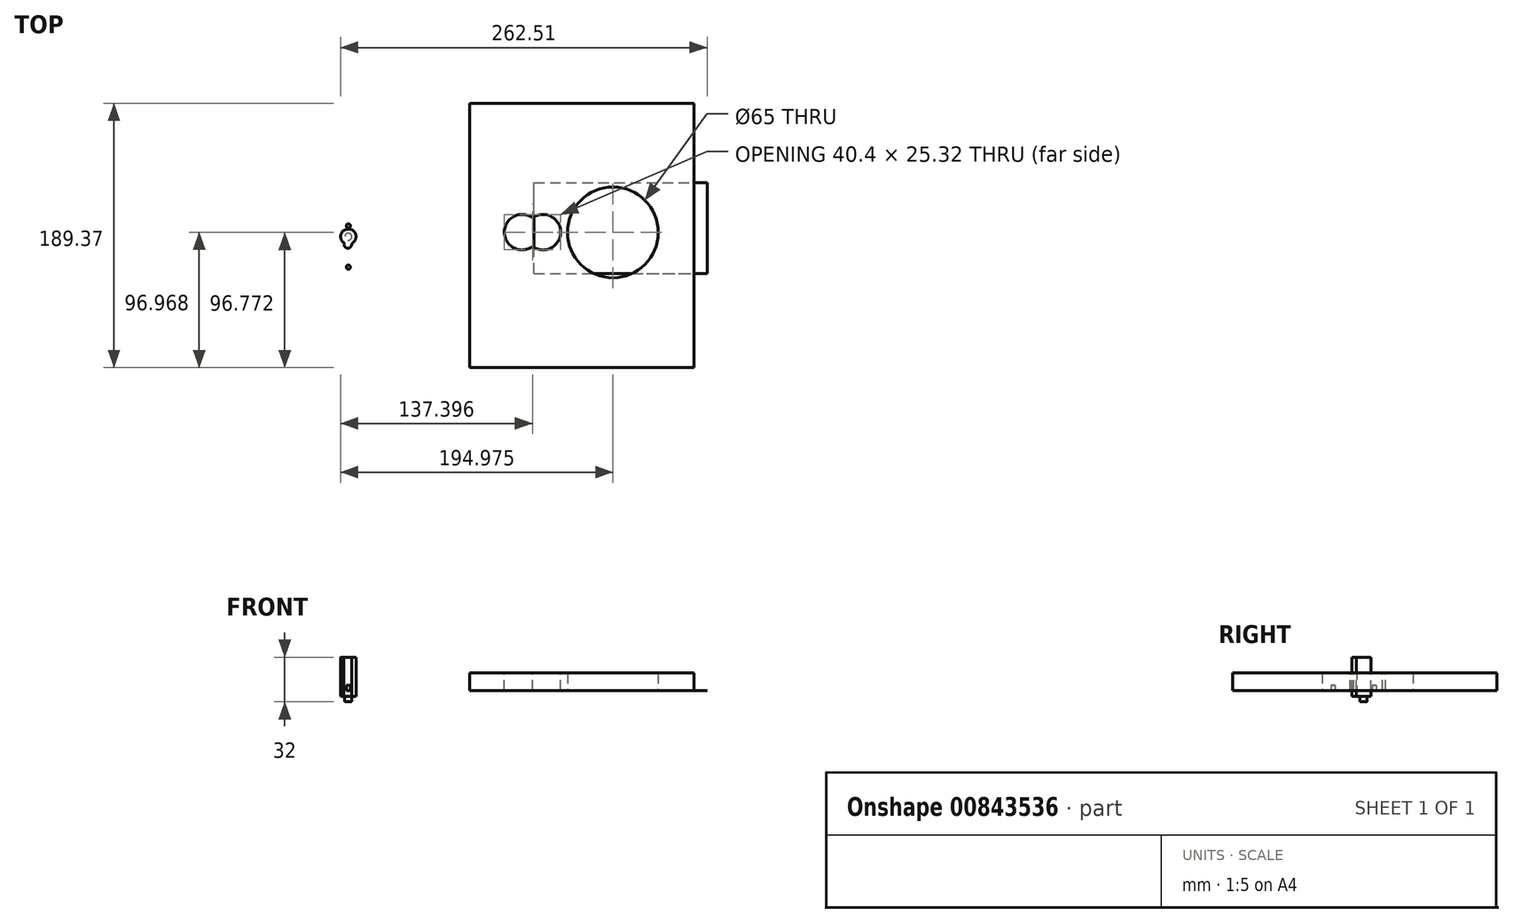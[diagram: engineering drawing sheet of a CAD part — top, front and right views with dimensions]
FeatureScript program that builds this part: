
annotation { "Feature Type Name" : "Feature", "Feature Type Description" : "" }
export const myFeature = defineFeature(function(context is Context, id is Id, definition is map)
    precondition{}
    {
        {
            var Q0;
            Q0=qCreatedBy(makeId("Top.planeOp"),FACE);
            var sketch = newSketch(context, id + "F0", { "sketchPlane" : qUnion([Q0])});
            skLineSegment(sketch, "E0.bottom", {"start": v(-82.3, 95.52) * mm, "end": v(78.38, 95.52) * mm});
            skLineSegment(sketch, "E0.top", {"start": v(-82.3, -93.85) * mm, "end": v(78.38, -93.85) * mm});
            skLineSegment(sketch, "E0.left", {"start": v(-82.3, 95.52) * mm, "end": v(-82.3, -93.85) * mm});
            skLineSegment(sketch, "E0.right", {"start": v(78.38, 95.52) * mm, "end": v(78.38, -93.85) * mm});
            skCircle(sketch, "E1", {"center": v(20.28, 2.92) * mm, "radius": 32.5 * mm});
            skSolve(sketch);
        }
        {
            var Q0;
            Q0 = qSketchRegion(id + "F0", true);
            extrude(context, id + "F1", {"entities" : qUnion([Q0]), "depth" : 12.7 * mm, "offsetDistance" : 25 * mm});
        }
        {
            var Q0;
            Q0=qCreatedBy(makeId("Top.planeOp"),FACE);
            var sketch = newSketch(context, id + "F2", { "sketchPlane" : qUnion([Q0])});
            skLineSegment(sketch, "E2.bottom", {"start": v(-36.19, -26.45) * mm, "end": v(87.81, -26.45) * mm});
            skLineSegment(sketch, "E2.top", {"start": v(-36.19, 38.55) * mm, "end": v(87.81, 38.55) * mm});
            skLineSegment(sketch, "E2.left", {"start": v(-36.19, -26.45) * mm, "end": v(-36.19, 38.55) * mm});
            skLineSegment(sketch, "E2.right", {"start": v(87.81, -26.45) * mm, "end": v(87.81, 38.55) * mm});
            skSolve(sketch);
        }
        {
            var Q0;
            Q0 = qSketchRegion(id + "F2", true);
            extrude(context, id + "F3", {"entities" : qUnion([Q0]), "oppositeDirection" : true, "depth" : 3 / 203.2 * mm, "offsetDistance" : 25 * mm});
        }
        {
            var Q0;
            Q0=makeQuery(id+"F1.opExtrude","CAP_FACE",FACE,{"disambiguationData":[OSD([sQuery(id+"F0.wireOp",EDGE,"E0.bottom"),sQuery(id+"F0.wireOp",EDGE,"E0.top"),sQuery(id+"F0.wireOp",EDGE,"E0.left"),sQuery(id+"F0.wireOp",EDGE,"E0.right"),sQuery(id+"F0.wireOp",EDGE,"E1")])],"isStart":false});
            var sketch = newSketch(context, id + "F4", { "sketchPlane" : qUnion([Q0])});
            skCircle(sketch, "E3", {"center": v(-29.8, 3.12) * mm, "radius": 12.7 * mm});
            skLineSegment(sketch, "E4", {"start": v(20.28, 2.92) * mm, "end": v(-82.3, 2.92) * mm, "construction": true});
            skLineSegment(sketch, "E5", {"start": v(-29.8, 3.12) * mm, "end": v(-44.8, 3.12) * mm, "construction": true});
            skCircle(sketch, "E6.MirrorC", {"center": v(-44.8, 3.12) * mm, "radius": 12.7 * mm});
            skSolve(sketch);
        }
        {
            var Q0;
            {var subQ0=sQuery(id+"F4.wireOp",EDGE,"E6.MirrorC");var subQ1=sQuery(id+"F4.wireOp",EDGE,"E3");var subQ2=makeQuery(id+"F4.imprint","INTERSECT",VERTEX,{"disambiguationData":[OD(0.0)],"derivedFrom":[subQ1,subQ0]});Q0=makeQuery(id+"F4.imprint","IMPRINT",FACE,{"disambiguationData":[TD([[makeQuery(id+"F4.imprint","IMPRINT",EDGE,{"disambiguationData":[TD([[subQ2,-1.0]])],"derivedFrom":subQ1}),1.0]])]});}
            var Q1;
            {var subQ0=sQuery(id+"F4.wireOp",EDGE,"E6.MirrorC");var subQ1=sQuery(id+"F4.wireOp",EDGE,"E3");var subQ2=makeQuery(id+"F4.imprint","INTERSECT",VERTEX,{"disambiguationData":[OD(0.0)],"derivedFrom":[subQ1,subQ0]});Q1=makeQuery(id+"F4.imprint","IMPRINT",FACE,{"disambiguationData":[TD([[makeQuery(id+"F4.imprint","IMPRINT",EDGE,{"disambiguationData":[TD([[subQ2,1.0]])],"derivedFrom":subQ1}),-1.0]])]});}
            var Q2;
            {var subQ0=sQuery(id+"F4.wireOp",EDGE,"E6.MirrorC");var subQ1=sQuery(id+"F4.wireOp",EDGE,"E3");var subQ2=makeQuery(id+"F4.imprint","INTERSECT",VERTEX,{"disambiguationData":[OD(0.0)],"derivedFrom":[subQ1,subQ0]});Q2=makeQuery(id+"F4.imprint","IMPRINT",FACE,{"disambiguationData":[TD([[makeQuery(id+"F4.imprint","IMPRINT",EDGE,{"disambiguationData":[TD([[subQ2,1.0]])],"derivedFrom":subQ1}),1.0]])]});}
            var Q3;
            Q3=makeQuery(id+"F1.opExtrude","CAP_FACE",FACE,{"disambiguationData":[OSD([sQuery(id+"F0.wireOp",EDGE,"E0.bottom"),sQuery(id+"F0.wireOp",EDGE,"E0.top"),sQuery(id+"F0.wireOp",EDGE,"E0.left"),sQuery(id+"F0.wireOp",EDGE,"E0.right"),sQuery(id+"F0.wireOp",EDGE,"E1")])],"isStart":true});
            extrude(context, id + "F5", {"entities" : qUnion([Q0, Q1, Q2]), "operationType" : NewBodyOperationType.REMOVE, "endBound" : BoundingType.UP_TO_SURFACE, "oppositeDirection" : true, "depth" : 25 * mm, "endBoundEntityFace" : qUnion([Q3]), "offsetDistance" : 25 * mm});
        }
        {
            var Q0;
            Q0=qCreatedBy(makeId("Top.planeOp"),FACE);
            var sketch = newSketch(context, id + "F6", { "sketchPlane" : qUnion([Q0])});
            skLineSegment(sketch, "E7.bottom", {"start": v(-175.2, 8.86) * mm, "end": v(-163.2, 8.86) * mm});
            skLineSegment(sketch, "E7.top", {"start": v(-175.2, -23.14) * mm, "end": v(-163.2, -23.14) * mm});
            skLineSegment(sketch, "E7.left", {"start": v(-175.2, 8.86) * mm, "end": v(-175.2, -23.14) * mm});
            skLineSegment(sketch, "E7.right", {"start": v(-163.2, 8.86) * mm, "end": v(-163.2, -23.14) * mm});
            skCircle(sketch, "E8", {"center": v(-169.2, -0.14) * mm, "radius": 5.5 * mm});
            skCircle(sketch, "E9", {"center": v(-169.57, -5.63) * mm, "radius": 2.75 * mm});
            skLineSegment(sketch, "E10", {"start": v(-169.2, 8.86) * mm, "end": v(-169.2, -23.14) * mm, "construction": true});
            skCircle(sketch, "E11", {"center": v(-169.2, 7.65) * mm, "radius": 1.5 * mm});
            skLineSegment(sketch, "E12", {"start": v(-175.2, -7.14) * mm, "end": v(-163.2, -7.14) * mm, "construction": true});
            skCircle(sketch, "E13.MirrorC", {"center": v(-169.2, -21.94) * mm, "radius": 1.5 * mm});
            skCircle(sketch, "E14", {"center": v(-169.2, -0.14) * mm, "radius": 2.5 * mm});
            skSolve(sketch);
        }
        {
            var Q0;
            Q0 = qSketchRegion(id + "F6", true);
            var Q1;
            Q1=makeQuery(id+"F6.imprint","IMPRINT",FACE,{"disambiguationData":[TD([[makeQuery(id+"F6.imprint","IMPRINT",EDGE,{"derivedFrom":sQuery(id+"F6.wireOp",EDGE,"E14")}),-1.0]])]});
            var Q2;
            Q2=makeQuery(id+"F6.imprint","IMPRINT",FACE,{"disambiguationData":[TD([[makeQuery(id+"F6.imprint","IMPRINT",EDGE,{"derivedFrom":sQuery(id+"F6.wireOp",EDGE,"E14")}),1.0]])]});
            var Q3;
            {var subQ0=sQuery(id+"F6.wireOp",EDGE,"E9");var subQ1=sQuery(id+"F6.wireOp",EDGE,"E8");var subQ2=makeQuery(id+"F6.imprint","INTERSECT",VERTEX,{"disambiguationData":[OD(0.0)],"derivedFrom":[subQ1,subQ0]});Q3=makeQuery(id+"F6.imprint","IMPRINT",FACE,{"disambiguationData":[TD([[makeQuery(id+"F6.imprint","IMPRINT",EDGE,{"disambiguationData":[TD([[subQ2,-1.0]])],"derivedFrom":subQ1}),-1.0]])]});}
            var Q4;
            {var subQ0=sQuery(id+"F6.wireOp",EDGE,"E9");var subQ1=sQuery(id+"F6.wireOp",EDGE,"E8");var subQ2=makeQuery(id+"F6.imprint","INTERSECT",VERTEX,{"disambiguationData":[OD(0.0)],"derivedFrom":[subQ1,subQ0]});Q4=makeQuery(id+"F6.imprint","IMPRINT",FACE,{"disambiguationData":[TD([[makeQuery(id+"F6.imprint","IMPRINT",EDGE,{"disambiguationData":[TD([[subQ2,-1.0]])],"derivedFrom":subQ1}),1.0]])]});}
            extrude(context, id + "F7", {"entities" : qUnion([Q0, Q1, Q2, Q3, Q4]), "depth" : 24 * mm, "offsetDistance" : 25 * mm});
        }
        {
            var Q0;
            Q0=makeQuery(id+"F6.imprint","IMPRINT",FACE,{"disambiguationData":[TD([[makeQuery(id+"F6.imprint","IMPRINT",EDGE,{"derivedFrom":sQuery(id+"F6.wireOp",EDGE,"E14")}),-1.0]])]});
            var Q1;
            {var subQ0=sQuery(id+"F6.wireOp",EDGE,"E9");var subQ1=sQuery(id+"F6.wireOp",EDGE,"E8");var subQ2=makeQuery(id+"F6.imprint","INTERSECT",VERTEX,{"disambiguationData":[OD(0.0)],"derivedFrom":[subQ1,subQ0]});Q1=makeQuery(id+"F6.imprint","IMPRINT",FACE,{"disambiguationData":[TD([[makeQuery(id+"F6.imprint","IMPRINT",EDGE,{"disambiguationData":[TD([[subQ2,-1.0]])],"derivedFrom":subQ1}),-1.0]])]});}
            var Q2;
            {var subQ0=sQuery(id+"F6.wireOp",EDGE,"E9");var subQ1=sQuery(id+"F6.wireOp",EDGE,"E8");var subQ2=makeQuery(id+"F6.imprint","INTERSECT",VERTEX,{"disambiguationData":[OD(0.0)],"derivedFrom":[subQ1,subQ0]});Q2=makeQuery(id+"F6.imprint","IMPRINT",FACE,{"disambiguationData":[TD([[makeQuery(id+"F6.imprint","IMPRINT",EDGE,{"disambiguationData":[TD([[subQ2,-1.0]])],"derivedFrom":subQ1}),1.0]])]});}
            extrude(context, id + "F8", {"entities" : qUnion([Q0, Q1, Q2]), "operationType" : NewBodyOperationType.ADD, "oppositeDirection" : true, "depth" : 4 * mm, "offsetDistance" : 25 * mm});
        }
        {
            var Q0;
            Q0=makeQuery(id+"F6.imprint","IMPRINT",FACE,{"disambiguationData":[TD([[makeQuery(id+"F6.imprint","IMPRINT",EDGE,{"derivedFrom":sQuery(id+"F6.wireOp",EDGE,"E14")}),1.0]])]});
            extrude(context, id + "F9", {"entities" : qUnion([Q0]), "operationType" : NewBodyOperationType.ADD, "oppositeDirection" : true, "depth" : 8 * mm, "offsetDistance" : 25 * mm});
        }
        {
            var Q0;
            Q0=makeQuery(id+"F7.opExtrude","CAP_FACE",FACE,{"disambiguationData":[OSD([sQuery(id+"F6.wireOp",EDGE,"E7.bottom"),sQuery(id+"F6.wireOp",EDGE,"E7.top"),sQuery(id+"F6.wireOp",EDGE,"E7.left"),sQuery(id+"F6.wireOp",EDGE,"E7.right"),sQuery(id+"F6.wireOp",EDGE,"E11"),sQuery(id+"F6.wireOp",EDGE,"E13.MirrorC")])],"isStart":false});
            var sketch = newSketch(context, id + "F10", { "sketchPlane" : qUnion([Q0])});
            skLineSegment(sketch, "E15", {"start": v(-163.2, 5.43) * mm, "end": v(-175.2, 5.43) * mm});
            skLineSegment(sketch, "E16", {"start": v(-163.2, -19.64) * mm, "end": v(-175.2, -19.64) * mm});
            skSolve(sketch);
        }
        {
            var Q0;
            Q0 = qSketchRegion(id + "F10", true);
            var Q1;
            {var subQ2=sQuery(id+"F10.wireOp",EDGE,"E15");Q1=makeQuery(id+"F10.imprint","IMPRINT",FACE,{"disambiguationData":[TD([[makeQuery(id+"F10.imprint","IMPRINT",EDGE,{"derivedFrom":subQ2}),-1.0]])]});}
            var Q2;
            {var subQ2=sQuery(id+"F10.wireOp",EDGE,"E16");Q2=makeQuery(id+"F10.imprint","IMPRINT",FACE,{"disambiguationData":[TD([[makeQuery(id+"F10.imprint","IMPRINT",EDGE,{"derivedFrom":subQ2}),1.0]])]});}
            extrude(context, id + "F11", {"entities" : qUnion([Q0, Q1, Q2]), "operationType" : NewBodyOperationType.REMOVE, "oppositeDirection" : true, "depth" : 20 * mm, "offsetDistance" : 25 * mm});
        }
        {
            var Q0;
            {var subQ0=sQuery(id+"F6.wireOp",EDGE,"E11");var subQ1=sQuery(id+"F6.wireOp",EDGE,"E7.bottom");var subQ2=makeQuery(id+"F6.imprint","INTERSECT",VERTEX,{"disambiguationData":[OD(0.0)],"derivedFrom":[subQ1,subQ0]});Q0=makeQuery(id+"F6.imprint","IMPRINT",FACE,{"disambiguationData":[TD([[makeQuery(id+"F6.imprint","IMPRINT",EDGE,{"disambiguationData":[TD([[subQ2,-1.0]])],"derivedFrom":subQ1}),-1.0]])]});}
            var Q1;
            {var subQ0=sQuery(id+"F6.wireOp",EDGE,"E13.MirrorC");var subQ1=sQuery(id+"F6.wireOp",EDGE,"E7.top");var subQ2=makeQuery(id+"F6.imprint","INTERSECT",VERTEX,{"disambiguationData":[OD(0.0)],"derivedFrom":[subQ1,subQ0]});Q1=makeQuery(id+"F6.imprint","IMPRINT",FACE,{"disambiguationData":[TD([[makeQuery(id+"F6.imprint","IMPRINT",EDGE,{"disambiguationData":[TD([[subQ2,-1.0]])],"derivedFrom":subQ1}),1.0]])]});}
            var Q2;
            {var subQ0=sQuery(id+"F6.wireOp",EDGE,"E13.MirrorC");var subQ1=sQuery(id+"F6.wireOp",EDGE,"E7.top");var subQ2=makeQuery(id+"F6.imprint","INTERSECT",VERTEX,{"disambiguationData":[OD(0.0)],"derivedFrom":[subQ1,subQ0]});Q2=makeQuery(id+"F6.imprint","IMPRINT",FACE,{"disambiguationData":[TD([[makeQuery(id+"F6.imprint","IMPRINT",EDGE,{"disambiguationData":[TD([[subQ2,-1.0]])],"derivedFrom":subQ1}),-1.0]])]});}
            var Q3;
            {var subQ0=sQuery(id+"F6.wireOp",EDGE,"E11");var subQ1=sQuery(id+"F6.wireOp",EDGE,"E7.bottom");var subQ2=makeQuery(id+"F6.imprint","INTERSECT",VERTEX,{"disambiguationData":[OD(0.0)],"derivedFrom":[subQ1,subQ0]});Q3=makeQuery(id+"F6.imprint","IMPRINT",FACE,{"disambiguationData":[TD([[makeQuery(id+"F6.imprint","IMPRINT",EDGE,{"disambiguationData":[TD([[subQ2,-1.0]])],"derivedFrom":subQ1}),1.0]])]});}
            extrude(context, id + "F12", {"entities" : qUnion([Q0, Q1, Q2, Q3]), "operationType" : NewBodyOperationType.REMOVE, "endBound" : BoundingType.UP_TO_NEXT, "depth" : 25 * mm, "offsetDistance" : 25 * mm});
        }
    });
